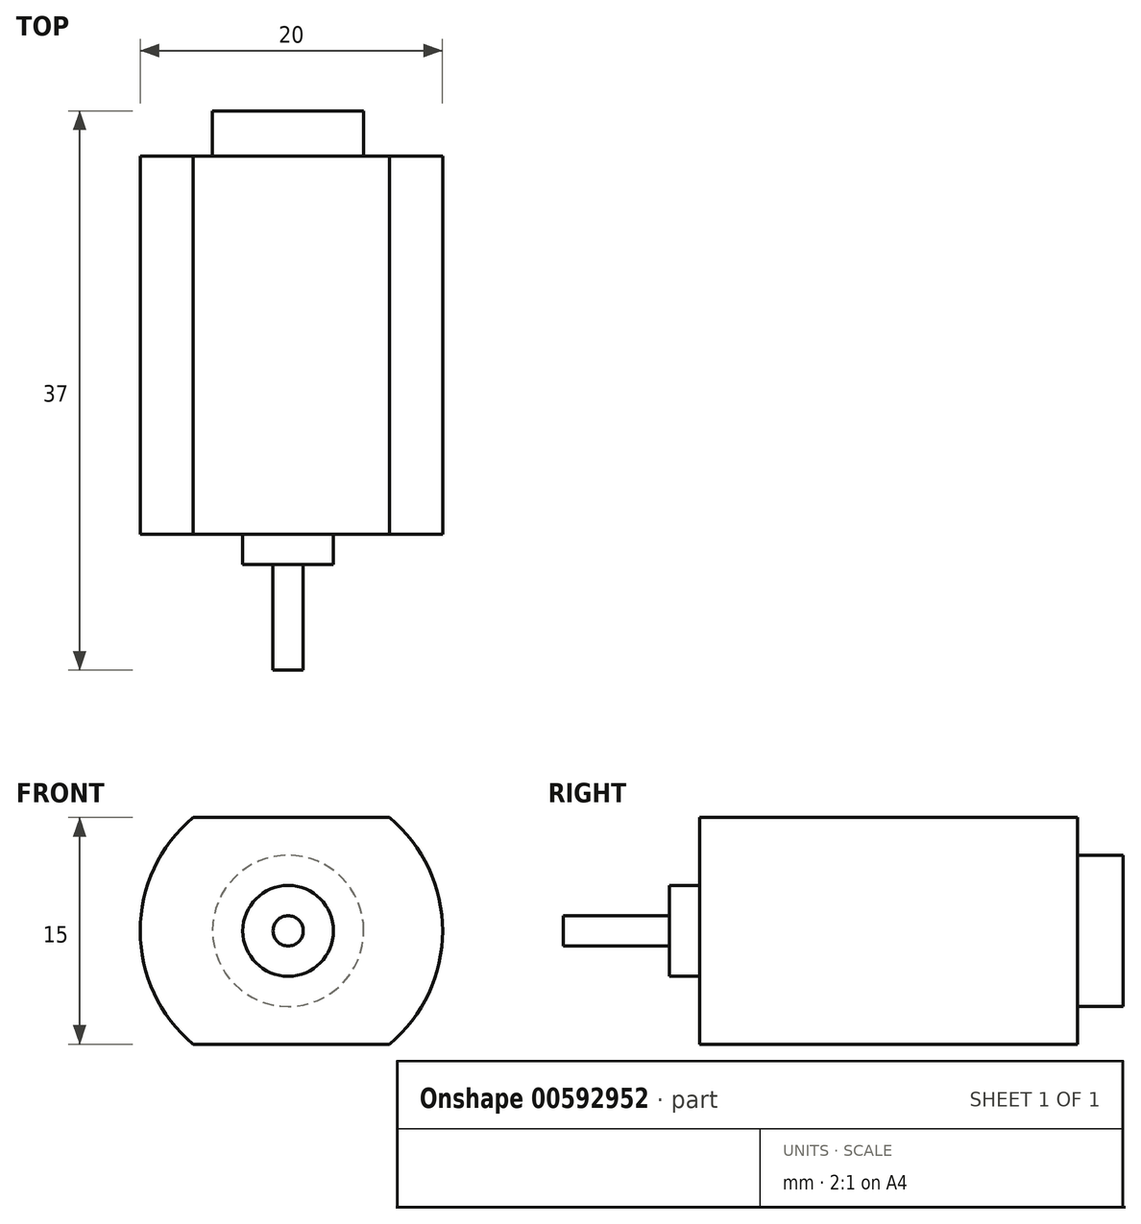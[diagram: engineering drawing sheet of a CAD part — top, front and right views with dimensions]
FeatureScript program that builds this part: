
annotation { "Feature Type Name" : "Feature", "Feature Type Description" : "" }
export const myFeature = defineFeature(function(context is Context, id is Id, definition is map)
    precondition{}
    {
        {
            var Q0;
            Q0=qCreatedBy(makeId("Front.planeOp"),FACE);
            var sketch = newSketch(context, id + "F0", { "sketchPlane" : qUnion([Q0])});
            skLineSegment(sketch, "E0", {"start": v(4.37, 11.59) * mm, "end": v(17.37, 11.59) * mm});
            skLineSegment(sketch, "E1", {"start": v(4.37, -3.41) * mm, "end": v(17.37, -3.41) * mm});
            skArc(sketch, "E2", {"start": v(17.37, -3.41) * mm, "mid": v(20.87, 4.09) * mm, "end": v(17.37, 11.59) * mm});
            skArc(sketch, "E3", {"start": v(4.37, 11.59) * mm, "mid": v(0.87, 4.09) * mm, "end": v(4.37, -3.41) * mm});
            skLineSegment(sketch, "E4", {"start": v(0.87, 4.09) * mm, "end": v(20.87, 4.09) * mm, "construction": true});
            skSolve(sketch);
        }
        {
            var Q0;
            Q0=makeQuery(id+"F0.imprint","IMPRINT",FACE,{"disambiguationData":[TD([[makeQuery(id+"F0.imprint","IMPRINT",EDGE,{"derivedFrom":sQuery(id+"F0.wireOp",EDGE,"E0")}),-1.0]])]});
            extrude(context, id + "F1", {"entities" : qUnion([Q0]), "depth" : 25 * mm, "offsetDistance" : 25 * mm});
        }
        {
            var Q0;
            Q0=makeQuery(id+"F1.opExtrude","CAP_FACE",FACE,{"disambiguationData":[OSD([sQuery(id+"F0.wireOp",EDGE,"E0"),sQuery(id+"F0.wireOp",EDGE,"E1"),sQuery(id+"F0.wireOp",EDGE,"E2"),sQuery(id+"F0.wireOp",EDGE,"E3")])],"isStart":false});
            var sketch = newSketch(context, id + "F2", { "sketchPlane" : qUnion([Q0])});
            skCircle(sketch, "E5", {"center": v(10.66, 4.09) * mm, "radius": 3 * mm});
            skCircle(sketch, "E6", {"center": v(10.66, 4.09) * mm, "radius": 1 * mm});
            skSolve(sketch);
        }
        {
            var Q0;
            Q0=makeQuery(id+"F2.imprint","IMPRINT",FACE,{"disambiguationData":[TD([[makeQuery(id+"F2.imprint","IMPRINT",EDGE,{"derivedFrom":sQuery(id+"F2.wireOp",EDGE,"E5")}),1.0]])]});
            extrude(context, id + "F3", {"entities" : qUnion([Q0]), "operationType" : NewBodyOperationType.ADD, "depth" : 2 * mm, "offsetDistance" : 25 * mm});
        }
        {
            var Q0;
            Q0=makeQuery(id+"F2.imprint","IMPRINT",FACE,{"disambiguationData":[TD([[makeQuery(id+"F2.imprint","IMPRINT",EDGE,{"derivedFrom":sQuery(id+"F2.wireOp",EDGE,"E6")}),1.0]])]});
            extrude(context, id + "F4", {"entities" : qUnion([Q0]), "operationType" : NewBodyOperationType.ADD, "depth" : 9 * mm, "offsetDistance" : 25 * mm});
        }
        {
            var Q0;
            Q0=makeQuery(id+"F1.opExtrude","CAP_FACE",FACE,{"disambiguationData":[OSD([sQuery(id+"F0.wireOp",EDGE,"E0"),sQuery(id+"F0.wireOp",EDGE,"E1"),sQuery(id+"F0.wireOp",EDGE,"E2"),sQuery(id+"F0.wireOp",EDGE,"E3")])],"isStart":true});
            var sketch = newSketch(context, id + "F5", { "sketchPlane" : qUnion([Q0])});
            skCircle(sketch, "E7", {"center": v(-10.66, 4.09) * mm, "radius": 5 * mm});
            skSolve(sketch);
        }
        {
            var Q0;
            Q0=makeQuery(id+"F5.imprint","IMPRINT",FACE,{"disambiguationData":[TD([[makeQuery(id+"F5.imprint","IMPRINT",EDGE,{"derivedFrom":sQuery(id+"F5.wireOp",EDGE,"E7")}),1.0]])]});
            extrude(context, id + "F6", {"entities" : qUnion([Q0]), "operationType" : NewBodyOperationType.ADD, "depth" : 3 * mm, "offsetDistance" : 25 * mm});
        }
    });
